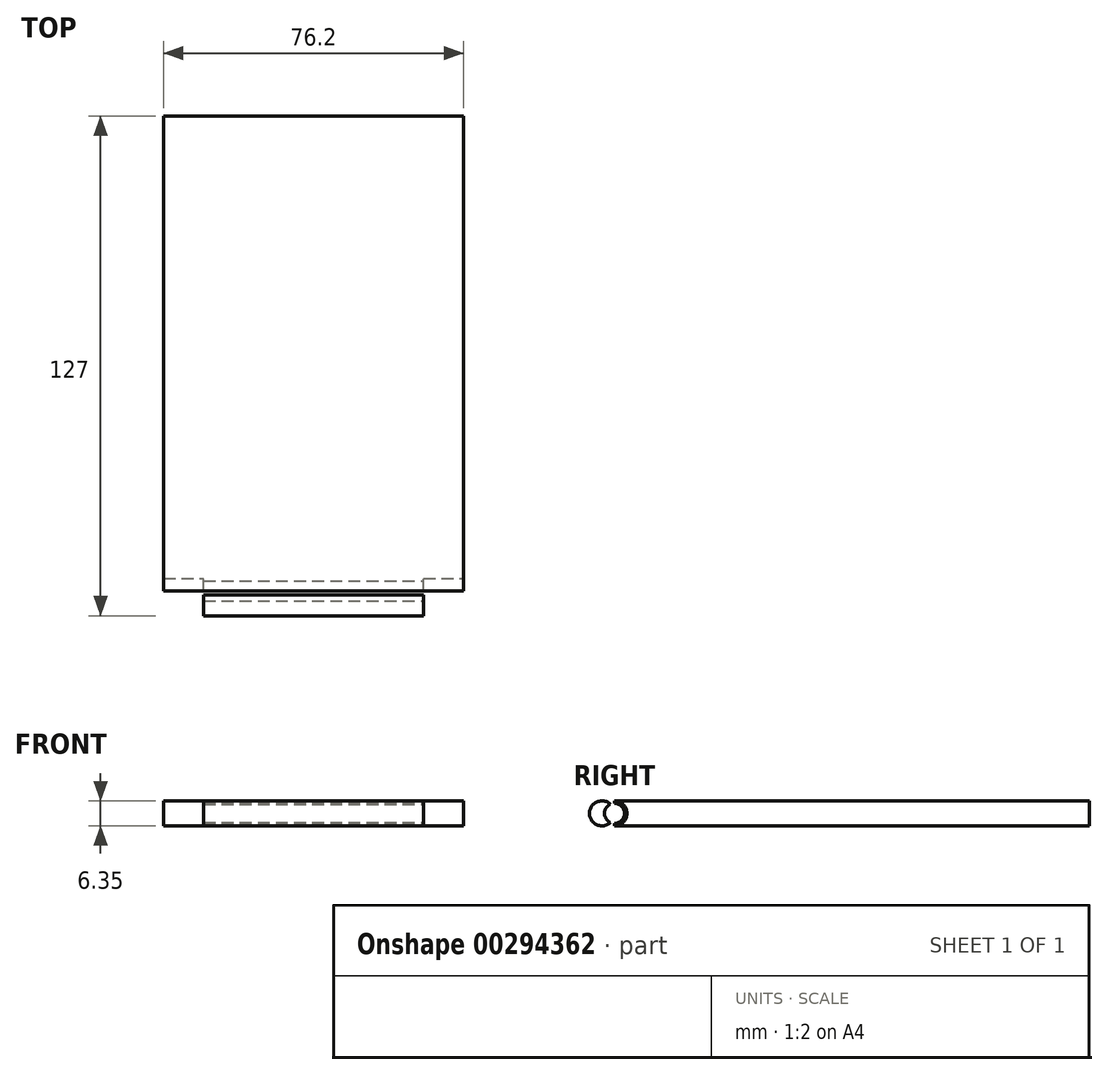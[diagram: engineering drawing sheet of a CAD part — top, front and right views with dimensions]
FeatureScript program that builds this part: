
annotation { "Feature Type Name" : "Feature", "Feature Type Description" : "" }
export const myFeature = defineFeature(function(context is Context, id is Id, definition is map)
    precondition{}
    {
        {
            var Q0;
            Q0=qCreatedBy(makeId("Top.planeOp"),FACE);
            var sketch = newSketch(context, id + "F0", { "sketchPlane" : qUnion([Q0])});
            skLineSegment(sketch, "E0.bottom", {"start": v(38.1, -63.5) * mm, "end": v(-38.1, -63.5) * mm});
            skLineSegment(sketch, "E0.top", {"start": v(38.1, 63.5) * mm, "end": v(-38.1, 63.5) * mm});
            skLineSegment(sketch, "E0.left", {"start": v(38.1, -63.5) * mm, "end": v(38.1, 63.5) * mm});
            skLineSegment(sketch, "E0.right", {"start": v(-38.1, -63.5) * mm, "end": v(-38.1, 63.5) * mm});
            skPoint(sketch, "E0.middle", {"position": v(0, 0) * mm});
            skSolve(sketch);
        }
        {
            var Q0;
            Q0 = qSketchRegion(id + "F0", true);
            extrude(context, id + "F1", {"entities" : qUnion([Q0]), "depth" : 6.35 * mm});
        }
        {
            var Q0;
            Q0=makeQuery(id+"F1.opExtrude","CAP_FACE",FACE,{"disambiguationData":[OSD([sQuery(id+"F0.wireOp",EDGE,"E0.bottom"),sQuery(id+"F0.wireOp",EDGE,"E0.top"),sQuery(id+"F0.wireOp",EDGE,"E0.left"),sQuery(id+"F0.wireOp",EDGE,"E0.right")])],"isStart":false});
            var sketch = newSketch(context, id + "F2", { "sketchPlane" : qUnion([Q0])});
            skLineSegment(sketch, "E1.bottom", {"start": v(-38.1, -63.5) * mm, "end": v(-27.94, -63.5) * mm});
            skLineSegment(sketch, "E1.top", {"start": v(-38.1, -57.15) * mm, "end": v(-27.94, -57.15) * mm});
            skLineSegment(sketch, "E1.left", {"start": v(-38.1, -63.5) * mm, "end": v(-38.1, -57.15) * mm});
            skLineSegment(sketch, "E1.right", {"start": v(-27.94, -63.5) * mm, "end": v(-27.94, -57.15) * mm});
            skLineSegment(sketch, "E2.MirrorCS", {"start": v(38.1, -63.5) * mm, "end": v(38.1, -57.15) * mm});
            skLineSegment(sketch, "E3.MirrorCS", {"start": v(38.1, -63.5) * mm, "end": v(27.94, -63.5) * mm});
            skLineSegment(sketch, "E4.MirrorCS", {"start": v(27.94, -63.5) * mm, "end": v(27.94, -57.15) * mm});
            skLineSegment(sketch, "E5.MirrorCS", {"start": v(38.1, -57.15) * mm, "end": v(27.94, -57.15) * mm});
            skSolve(sketch);
        }
        {
            var Q0;
            Q0 = qSketchRegion(id + "F2", true);
            var Q1;
            Q1=sQuery(id+"F2.wireOp",EDGE,"E1.left");
            var Q2;
            Q2=sQuery(id+"F2.wireOp",EDGE,"E2.MirrorCS");
            var Q3;
            Q3=sQuery(id+"F2.wireOp",EDGE,"E1.right");
            var Q4;
            Q4=sQuery(id+"F2.wireOp",EDGE,"E1.bottom");
            var Q5;
            Q5=sQuery(id+"F2.wireOp",EDGE,"E1.top");
            var Q6;
            Q6=sQuery(id+"F2.wireOp",EDGE,"E5.MirrorCS");
            var Q7;
            Q7=sQuery(id+"F2.wireOp",EDGE,"E3.MirrorCS");
            var Q8;
            Q8=sQuery(id+"F2.wireOp",EDGE,"E4.MirrorCS");
            extrude(context, id + "F3", {"entities" : qUnion([Q0]), "operationType" : NewBodyOperationType.REMOVE, "surfaceEntities" : qUnion([Q1, Q2, Q3, Q4, Q5, Q6, Q7, Q8]), "oppositeDirection" : true, "depth" : 25.4 * mm});
        }
        {
            var Q0;
            Q0=makeQuery(id+"F3.boolean.opBoolean","COPY",FACE,{"derivedFrom":makeQuery(id+"F3.opExtrude","SWEPT_FACE",FACE,{"disambiguationData":[OSD([sQuery(id+"F2.wireOp",EDGE,"E1.right")])]})});
            var sketch = newSketch(context, id + "F4", { "sketchPlane" : qUnion([Q0])});
            skCircle(sketch, "E6", {"center": v(60.33, 3.17) * mm, "radius": 3.18 * mm});
            skPoint(sketch, "E6.centerSnap0", {"position": v(63.5, 3.17) * mm});
            skSolve(sketch);
        }
        {
            var Q0;
            {var subQ0=sQuery(id+"F4.wireOp",EDGE,"E6");var subQ1=sQuery(id+"F2.wireOp",EDGE,"E1.right");var subQ2=makeQuery(id+"F3.boolean.opBoolean","COPY",EDGE,{"derivedFrom":makeQuery(id+"F3.opExtrude","CAP_EDGE",EDGE,{"disambiguationData":[OSD([subQ1])],"isStart":true})});var subQ3=makeQuery(id+"F4.imprint","INTERSECT",VERTEX,{"derivedFrom":[subQ2,subQ0]});Q0=makeQuery(id+"F4.imprint","IMPRINT",FACE,{"disambiguationData":[TD([[makeQuery(id+"F4.imprint","IMPRINT",EDGE,{"disambiguationData":[TD([[subQ3,1.0]])],"derivedFrom":subQ0}),-1.0]])]});}
            var Q1;
            {var subQ0=sQuery(id+"F4.wireOp",EDGE,"E6");var subQ1=sQuery(id+"F2.wireOp",EDGE,"E1.right");var subQ2=sQuery(id+"F0.wireOp",EDGE,"E0.bottom");var subQ3=makeQuery(id+"F3.boolean.opBoolean","COPY",EDGE,{"derivedFrom":makeQuery(id+"F3.opExtrude","SWEPT_EDGE",EDGE,{"disambiguationData":[OSD([subQ2,sQuery(id+"F2.wireOp",EDGE,"E1.bottom"),subQ1])]})});var subQ4=makeQuery(id+"F4.imprint","INTERSECT",VERTEX,{"derivedFrom":[subQ3,subQ0]});Q1=makeQuery(id+"F4.imprint","IMPRINT",FACE,{"disambiguationData":[TD([[makeQuery(id+"F4.imprint","IMPRINT",EDGE,{"disambiguationData":[TD([[subQ4,1.0]])],"derivedFrom":subQ0}),-1.0]])]});}
            extrude(context, id + "F5", {"entities" : qUnion([Q0, Q1]), "operationType" : NewBodyOperationType.REMOVE, "oppositeDirection" : true, "depth" : 76.2 * mm});
        }
        {
            var Q0;
            Q0=qCreatedBy(makeId("Right.planeOp"),FACE);
            var sketch = newSketch(context, id + "F6", { "sketchPlane" : qUnion([Q0])});
            skArc(sketch, "E7", {"start": v(-57.15, 0) * mm, "mid": v(-53.98, 3.17) * mm, "end": v(-57.15, 6.35) * mm});
            skLineSegment(sketch, "E8", {"start": v(-57.15, 6.35) * mm, "end": v(-57.15, 0) * mm});
            skSolve(sketch);
        }
        {
            var Q0;
            Q0 = qSketchRegion(id + "F6", true);
            extrude(context, id + "F7", {"entities" : qUnion([Q0]), "operationType" : NewBodyOperationType.REMOVE, "endBound" : BoundingType.SYMMETRIC, "oppositeDirection" : true, "depth" : 76.2 * mm});
        }
        {
            var Q0;
            Q0=qCreatedBy(makeId("Top.planeOp"),FACE);
            var sketch = newSketch(context, id + "F8", { "sketchPlane" : qUnion([Q0])});
            skLineSegment(sketch, "E9.bottom", {"start": v(27.94, -57.15) * mm, "end": v(-27.94, -57.15) * mm});
            skLineSegment(sketch, "E9.top", {"start": v(27.94, -47.23) * mm, "end": v(-27.94, -47.23) * mm});
            skLineSegment(sketch, "E9.left", {"start": v(27.94, -57.15) * mm, "end": v(27.94, -47.23) * mm});
            skLineSegment(sketch, "E9.right", {"start": v(-27.94, -57.15) * mm, "end": v(-27.94, -47.23) * mm});
            skSolve(sketch);
        }
        {
            var Q0;
            Q0 = qSketchRegion(id + "F8", true);
            extrude(context, id + "F9", {"entities" : qUnion([Q0]), "operationType" : NewBodyOperationType.ADD, "depth" : 6.35 * mm});
        }
        {
            var Q0;
            Q0=qCreatedBy(makeId("Right.planeOp"),FACE);
            var sketch = newSketch(context, id + "F10", { "sketchPlane" : qUnion([Q0])});
            skCircle(sketch, "E10", {"center": v(-57.15, 3.17) * mm, "radius": 3.18 * mm});
            skSolve(sketch);
        }
        {
            var Q0;
            Q0=qCreatedBy(makeId("Right.planeOp"),FACE);
            var sketch = newSketch(context, id + "F11", { "sketchPlane" : qUnion([Q0])});
            skCircle(sketch, "E11", {"center": v(-57.15, 3.17) * mm, "radius": 2.54 * mm});
            skSolve(sketch);
        }
        {
            var Q0;
            Q0 = qSketchRegion(id + "F11", true);
            extrude(context, id + "F12", {"entities" : qUnion([Q0]), "operationType" : NewBodyOperationType.REMOVE, "endBound" : BoundingType.SYMMETRIC, "oppositeDirection" : true, "depth" : 55.88 * mm});
        }
    });
